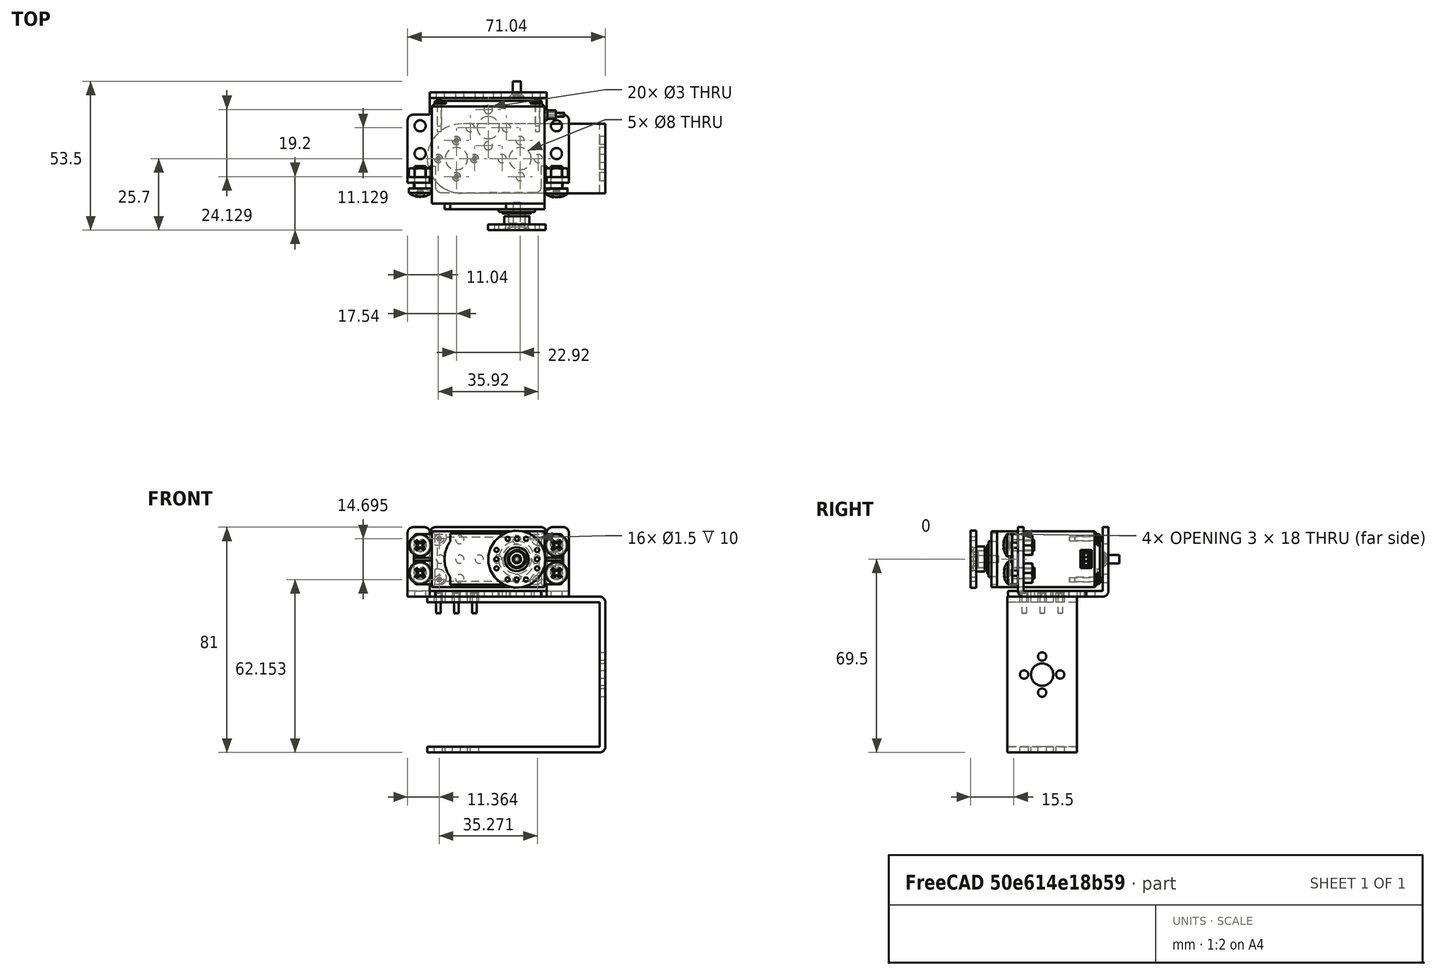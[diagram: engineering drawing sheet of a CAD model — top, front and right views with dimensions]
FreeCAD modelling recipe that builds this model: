
FCSTD DOCUMENT  (FreeCAD 0.19R24276 (Git))
Label: servo_con_union
License: All rights reserved
LicenseURL: http://en.wikipedia.org/wiki/All_rights_reserved
objects: Part::FeaturePython×17, App::FeaturePython×16, App::DocumentObjectGroup×2
note: 17 computed .brp shape members not serialized (recipe doc carries the construction recipe); baked Part::Feature solids carry a one-line shape summary decoded from their .brp

FEATURE [Part::FeaturePython] b_parte_servos_001_  label="parte_servos_001"  # a2plus imported part (geometry in sourceFile) (typed FeaturePython)
  Placement = pos=(0,0,0) rot=(0,0,1;3.14159rad)
  a2p_Version = V0.1
  fixedPosition = true
  objectType = a2pPart
  sourceFile = .\..\piezas\parte_servos.FCStd
  subassemblyImport = false
  timeLastImport = 1.62041e+09
  updateColors = true
FEATURE [Part::FeaturePython] b_tapa_001_  label="tapa_001"  # a2plus imported part (geometry in sourceFile) (typed FeaturePython)
  Placement = pos=(10.25,-31.5,13.5) rot=(-1,0.000384,0.000384;1.5708rad)
  a2p_Version = V0.1
  fixedPosition = false
  objectType = a2pPart
  sourceFile = .\..\piezas\tapa.FCStd
  subassemblyImport = false
  timeLastImport = 1.62041e+09
  updateColors = true
FEATURE [Part::FeaturePython] b_parte_union_001_  label="parte_union_001"  # a2plus imported part (geometry in sourceFile) (typed FeaturePython)
  Placement = pos=(42.04,-5.8,-28) rot=(0,-1,0;1.5708rad)
  a2p_Version = V0.1
  fixedPosition = false
  objectType = a2pPart
  sourceFile = .\..\piezas\parte_union.FCStd
  subassemblyImport = false
  timeLastImport = 1.62041e+09
  updateColors = true
FEATURE [App::FeaturePython] planeCoincident_003  label="planeCoincident_003__parte_union_001"  # a2plus constraint (typed FeaturePython)
  Object1 = b_parte_servos_001_
  Object2 = b_parte_union_001_
  ParentTreeObject = -> b_parte_servos_001_
  SubElement1 = Face8
  SubElement2 = Face20
  Suppressed = false
  Type = plane
  directionConstraint = 1
  offset = 0
FEATURE [App::FeaturePython] planeCoincident_003_mirror  label="planeCoincident_003__parte_servos_001"  # a2plus constraint (typed FeaturePython)
  Object1 = b_parte_servos_001_
  Object2 = b_parte_union_001_
  ParentTreeObject = -> b_parte_union_001_
  SubElement1 = Face8
  SubElement2 = Face20
  Suppressed = false
  Type = plane
  directionConstraint = 1
  offset = 0
FEATURE [App::FeaturePython] axisCoincident_004  label="axisCoincident_004__parte_servos_001"  # a2plus constraint (typed FeaturePython)
  Object1 = b_parte_union_001_
  Object2 = b_parte_servos_001_
  ParentTreeObject = -> b_parte_union_001_
  SubElement1 = Face35
  SubElement2 = Face62
  Suppressed = false
  Type = axial
  directionConstraint = 0
  lockRotation = false
FEATURE [App::FeaturePython] axisCoincident_004_mirror  label="axisCoincident_004__parte_union_001"  # a2plus constraint (typed FeaturePython)
  Object1 = b_parte_union_001_
  Object2 = b_parte_servos_001_
  ParentTreeObject = -> b_parte_servos_001_
  SubElement1 = Face35
  SubElement2 = Face62
  Suppressed = false
  Type = axial
  directionConstraint = 0
  lockRotation = false
FEATURE [App::FeaturePython] axisCoincident_005  label="axisCoincident_005__parte_servos_001"  # a2plus constraint (typed FeaturePython)
  Object1 = b_parte_union_001_
  Object2 = b_parte_servos_001_
  ParentTreeObject = -> b_parte_union_001_
  SubElement1 = Face37
  SubElement2 = Face61
  Suppressed = false
  Type = axial
  directionConstraint = 0
  lockRotation = false
FEATURE [App::FeaturePython] axisCoincident_005_mirror  label="axisCoincident_005__parte_union_001"  # a2plus constraint (typed FeaturePython)
  Object1 = b_parte_union_001_
  Object2 = b_parte_servos_001_
  ParentTreeObject = -> b_parte_servos_001_
  SubElement1 = Face37
  SubElement2 = Face61
  Suppressed = false
  Type = axial
  directionConstraint = 0
  lockRotation = false
FEATURE [Part::FeaturePython] Screw  label="M1.6x8-Screw"  # Fasteners workbench fastener (typed FeaturePython)
  Placement = pos=(-11.46,0.7,2) rot=(0,0,1;0rad)
  baseObject = -> b_parte_servos_001_ [Edge155]
  diameter = 1
  invert = false
  length = 4
  lengthCustom = 8
  matchOuter = true
  offset = 0
  thread = false
  type = 35
FEATURE [Part::FeaturePython] Screw001  label="M1.6x8-Screw004"  # Fasteners workbench fastener (typed FeaturePython)
  Placement = pos=(-17.96,-5.8,2) rot=(0,0,1;0rad)
  baseObject = -> b_parte_servos_001_ [Edge160]
  diameter = 1
  invert = false
  length = 4
  lengthCustom = 8
  matchOuter = true
  offset = 0
  thread = false
  type = 35
FEATURE [Part::FeaturePython] Screw002  label="M1.6x8-Screw005"  # Fasteners workbench fastener (typed FeaturePython)
  Placement = pos=(-11.46,-12.3,2) rot=(0,0,1;0rad)
  baseObject = -> b_parte_servos_001_ [Edge159]
  diameter = 1
  invert = false
  length = 4
  lengthCustom = 8
  matchOuter = true
  offset = 0
  thread = false
  type = 35
FEATURE [Part::FeaturePython] Screw003  label="M1.6x8-Screw006"  # Fasteners workbench fastener (typed FeaturePython)
  Placement = pos=(-4.96,-5.8,2) rot=(0,0,1;0rad)
  baseObject = -> b_parte_servos_001_ [Edge157]
  diameter = 1
  invert = false
  length = 4
  lengthCustom = 8
  matchOuter = true
  offset = 0
  thread = false
  type = 35
FEATURE [Part::FeaturePython] Screw004  label="M4x8-Screw"  # Fasteners workbench fastener (typed FeaturePython)
  Placement = pos=(24.5,-16.6843,18.5) rot=(1,0,0;1.5708rad)
  diameter = 6
  invert = false
  length = 12
  lengthCustom = 8
  matchOuter = true
  offset = 0
  thread = false
  type = 34
FEATURE [Part::FeaturePython] Screw005  label="M4x8-Screw004"  # Fasteners workbench fastener (typed FeaturePython)
  Placement = pos=(24.5,-16.5,8.5) rot=(1,0,0;1.5708rad)
  diameter = 6
  invert = false
  length = 12
  lengthCustom = 8
  matchOuter = true
  offset = 0
  thread = false
  type = 34
FEATURE [Part::FeaturePython] Screw006  label="M4x8-Screw005"  # Fasteners workbench fastener (typed FeaturePython)
  Placement = pos=(-24.5,-16.5,8.5) rot=(1,0,0;1.5708rad)
  diameter = 6
  invert = true
  length = 12
  lengthCustom = 8
  matchOuter = true
  offset = 0
  thread = false
  type = 34
FEATURE [Part::FeaturePython] Screw007  label="M4x8-Screw006"  # Fasteners workbench fastener (typed FeaturePython)
  Placement = pos=(-24.5,-16.5,18.5) rot=(1,0,0;1.5708rad)
  diameter = 6
  invert = true
  length = 12
  lengthCustom = 8
  matchOuter = true
  offset = 0
  thread = false
  type = 34
FEATURE [Part::FeaturePython] Nut  label="M4-Nut"  # Fasteners workbench fastener (typed FeaturePython)
  Placement = pos=(24.5,-12.5,18.5) rot=(-1,0,0;1.5708rad)
  baseObject = -> b_parte_servos_001_ [Edge192]
  diameter = 6
  invert = true
  matchOuter = true
  offset = 0
  thread = false
  type = 7
FEATURE [Part::FeaturePython] Nut001  label="M4-Nut004"  # Fasteners workbench fastener (typed FeaturePython)
  Placement = pos=(24.5,-12.5,8.5) rot=(-1,0,0;1.5708rad)
  baseObject = -> b_parte_servos_001_ [Edge193]
  diameter = 6
  invert = true
  matchOuter = true
  offset = 0
  thread = false
  type = 7
FEATURE [Part::FeaturePython] Nut002  label="M4-Nut005"  # Fasteners workbench fastener (typed FeaturePython)
  Placement = pos=(-24.5,-12.5,8.5) rot=(-1,0,0;1.5708rad)
  baseObject = -> b_parte_servos_001_ [Edge220]
  diameter = 6
  invert = true
  matchOuter = true
  offset = 0
  thread = false
  type = 7
FEATURE [Part::FeaturePython] Nut003  label="M4-Nut006"  # Fasteners workbench fastener (typed FeaturePython)
  Placement = pos=(-24.5,-12.5,18.5) rot=(-1,0,0;1.5708rad)
  baseObject = -> b_parte_servos_001_ [Edge219]
  diameter = 6
  invert = true
  matchOuter = true
  offset = 0
  thread = false
  type = 7
FEATURE [App::DocumentObjectGroup] Group001  label="tercas"
  Group = -> [Nut,Nut001,Nut002,Nut003]
FEATURE [Part::FeaturePython] Screw008  label="M3x6-Screw"  # Fasteners workbench fastener (typed FeaturePython)
  Placement = pos=(10.25,16,13.5) rot=(1,0,0;1.5708rad)
  baseObject = -> b_parte_servos_001_ [Edge83]
  diameter = 4
  invert = false
  length = 11
  lengthCustom = 6
  matchOuter = true
  offset = 0
  thread = false
  type = 35
FEATURE [App::DocumentObjectGroup] Group  label="tornillos"
  Group = -> [Screw,Screw001,Screw002,Screw003,Screw004,Screw005,Screw006,Screw007,Screw008]
FEATURE [Part::FeaturePython] b_servo_001_  label="servo_001"  # a2plus imported part (geometry in sourceFile) (typed FeaturePython)
  Placement = pos=(9.71781e-08,15,13.5) rot=(0,0.707107,-0.707107;3.14159rad)
  a2p_Version = V0.1
  fixedPosition = false
  objectType = a2pPart
  sourceFile = .\..\piezas\servo.FCStd
  subassemblyImport = false
  timeLastImport = 1.62041e+09
  updateColors = true
FEATURE [App::FeaturePython] planeCoincident_001  label="planeCoincident_001__parte_servos_001"  # a2plus constraint (typed FeaturePython)
  Object1 = b_servo_001_
  Object2 = b_parte_servos_001_
  ParentTreeObject = -> b_servo_001_
  SubElement1 = Face115
  SubElement2 = Face84
  Suppressed = false
  Type = plane
  directionConstraint = 1
  offset = 0
FEATURE [App::FeaturePython] planeCoincident_001_mirror  label="planeCoincident_001__servo_001"  # a2plus constraint (typed FeaturePython)
  Object1 = b_servo_001_
  Object2 = b_parte_servos_001_
  ParentTreeObject = -> b_parte_servos_001_
  SubElement1 = Face115
  SubElement2 = Face84
  Suppressed = false
  Type = plane
  directionConstraint = 1
  offset = 0
FEATURE [App::FeaturePython] axisCoincident_001  label="axisCoincident_001__servo_001"  # a2plus constraint (typed FeaturePython)
  Object1 = Screw006
  Object2 = b_servo_001_
  ParentTreeObject = -> Screw006
  SubElement1 = Face5
  SubElement2 = Face138
  Suppressed = false
  Type = axial
  directionConstraint = 1
  lockRotation = false
FEATURE [App::FeaturePython] axisCoincident_001_mirror  label="axisCoincident_001__M4x8-Screw005"  # a2plus constraint (typed FeaturePython)
  Object1 = Screw006
  Object2 = b_servo_001_
  ParentTreeObject = -> b_servo_001_
  SubElement1 = Face5
  SubElement2 = Face138
  Suppressed = false
  Type = axial
  directionConstraint = 1
  lockRotation = false
FEATURE [App::FeaturePython] axisCoincident_002  label="axisCoincident_002__servo_001"  # a2plus constraint (typed FeaturePython)
  Object1 = b_parte_servos_001_
  Object2 = b_servo_001_
  ParentTreeObject = -> b_parte_servos_001_
  SubElement1 = Face82
  SubElement2 = Face138
  Suppressed = false
  Type = axial
  directionConstraint = 0
  lockRotation = false
FEATURE [App::FeaturePython] axisCoincident_002_mirror  label="axisCoincident_002__parte_servos_001"  # a2plus constraint (typed FeaturePython)
  Object1 = b_parte_servos_001_
  Object2 = b_servo_001_
  ParentTreeObject = -> b_servo_001_
  SubElement1 = Face82
  SubElement2 = Face138
  Suppressed = false
  Type = axial
  directionConstraint = 0
  lockRotation = false
FEATURE [App::FeaturePython] axisCoincident_003  label="axisCoincident_003__servo_001"  # a2plus constraint (typed FeaturePython)
  Object1 = b_parte_servos_001_
  Object2 = b_servo_001_
  ParentTreeObject = -> b_parte_servos_001_
  SubElement1 = Face73
  SubElement2 = Face162
  Suppressed = false
  Type = axial
  directionConstraint = 0
  lockRotation = false
FEATURE [App::FeaturePython] axisCoincident_003_mirror  label="axisCoincident_003__parte_servos_001"  # a2plus constraint (typed FeaturePython)
  Object1 = b_parte_servos_001_
  Object2 = b_servo_001_
  ParentTreeObject = -> b_servo_001_
  SubElement1 = Face73
  SubElement2 = Face162
  Suppressed = false
  Type = axial
  directionConstraint = 0
  lockRotation = false
FEATURE [App::FeaturePython] axisCoincident_006  label="axisCoincident_006__parte_servos_001"  # a2plus constraint (typed FeaturePython)
  Object1 = Screw008
  Object2 = b_parte_servos_001_
  ParentTreeObject = -> Screw008
  SubElement1 = Face4
  SubElement2 = Face17
  Suppressed = false
  Type = axial
  directionConstraint = 1
  lockRotation = false
FEATURE [App::FeaturePython] axisCoincident_006_mirror  label="axisCoincident_006__M3x6-Screw"  # a2plus constraint (typed FeaturePython)
  Object1 = Screw008
  Object2 = b_parte_servos_001_
  ParentTreeObject = -> b_parte_servos_001_
  SubElement1 = Face4
  SubElement2 = Face17
  Suppressed = false
  Type = axial
  directionConstraint = 1
  lockRotation = false
